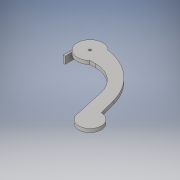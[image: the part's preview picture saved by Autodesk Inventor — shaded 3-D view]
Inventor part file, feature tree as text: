
AUTODESK INVENTOR PART (.ipt)
format: ipt  version: 2016 (Build 200138000, 138)  size: 180,736 bytes
history: native  units: in
note: dims shown in document units (in); Inventor stores cm internally (conversion verified against a paired STEP export)
features: sketch x10, extrude x9, fillet x2
ambient origin geometry x8: Origin, YZ Plane, XZ Plane, XY Plane, X Axis, Y Axis, Z Axis, Center Point
bodies: Solid1 (feature_tree)
feature tree (21):
  extrude  "Extrusion1"  Depth=0.75in
  extrude  "Extrusion2"  Depth=0.125in TaperAngle=0.0deg
  extrude  "Extrusion3"  Depth=0.3125in TaperAngle=0.0deg
  extrude  "Extrusion6"  Depth=0.45in TaperAngle=0.0deg
  extrude  "Extrusion7"  TaperAngle=157.5deg  [1 undecoded]
  sketch  "Sketch16"  dims[d62=1.0in d63=0.0in d84=45.0deg]
  extrude  "Extrusion16"  TaperAngle=45.0deg  [1 undecoded]
  extrude  "Extrusion17"  TaperAngle=0.0deg  [1 undecoded]
  extrude  "Extrusion20"  Depth=1.2in
  extrude  "Extrusion21"  Depth=0.125in TaperAngle=0.0deg
  fillet  "Fillet6"  [1 undecoded]
  fillet  "Fillet7"  Radius=1.25in
  sketch  "Sketch1"  dims[d0=0.9in d1=0.75in]
  sketch  "Sketch2"  dims[d2=0.25in d3=0.0in d4=0.125in d5=0.0in]
  sketch  "Sketch3"  dims[d6=0.0866in d7=0.3125in d8=0.0in]
  sketch  "Sketch6"  dims[d14=0.25in d15=0.0in d16=0.45in d17=0.0in]
  sketch  "Sketch7"  dims[d59=0.5in d60=0.0in d61=157.5deg]
  sketch  "Sketch17"  dims[d85=1.0in d86=0.0in]
  sketch  "Sketch18"  dims[d87=0.8in d88=1.2in]
  sketch  "Sketch21"  dims[d89=45.0deg d90=0.125in d91=0.0in d92=45.0deg d93=1.25in]
  sketch  "Sketch22"  dims[d94=1.0in d95=0.125in d96=0.0in d97=1.0in d98=2.0in]
note: 4 required parameter values undecoded (feature->parameter linkage not recoverable at this tier; creation-order binding heuristic only, values carry confidence <= 0.55)
